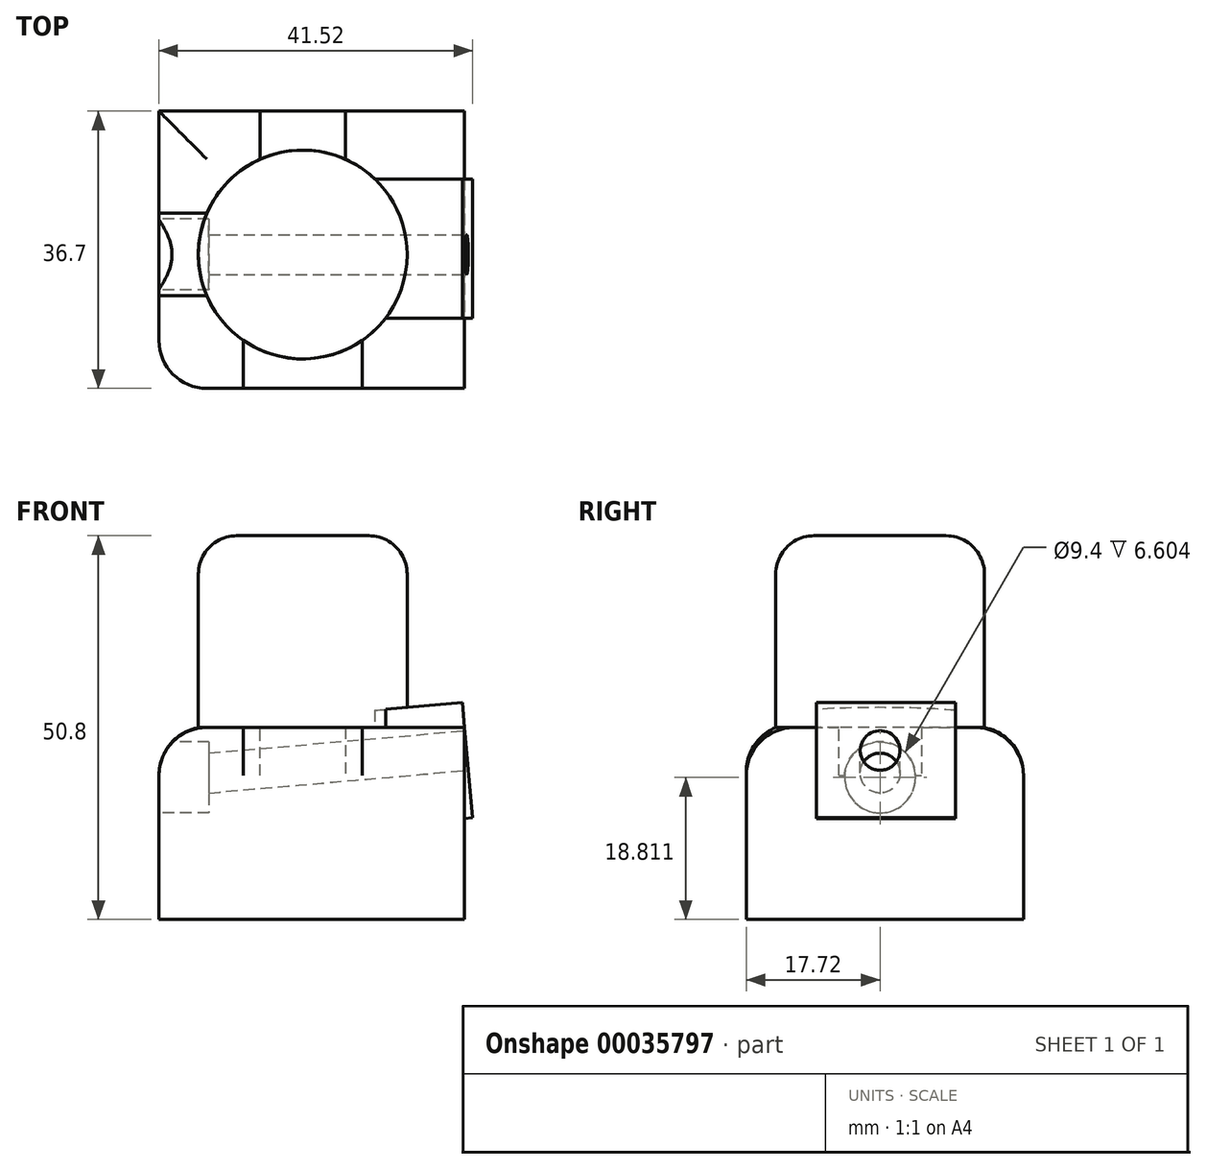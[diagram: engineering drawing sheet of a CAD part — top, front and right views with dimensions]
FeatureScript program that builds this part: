
annotation { "Feature Type Name" : "Feature", "Feature Type Description" : "" }
export const myFeature = defineFeature(function(context is Context, id is Id, definition is map)
    precondition{}
    {
        {
            var Q0;
            Q0=qCreatedBy(makeId("Top.planeOp"),FACE);
            var sketch = newSketch(context, id + "F0", { "sketchPlane" : qUnion([Q0])});
            skLineSegment(sketch, "E0.bottom", {"start": v(-50.18, -17.72) * mm, "end": v(-9.7, -17.72) * mm});
            skLineSegment(sketch, "E0.top", {"start": v(-50.18, 18.98) * mm, "end": v(-9.7, 18.98) * mm});
            skLineSegment(sketch, "E0.left", {"start": v(-50.18, -17.72) * mm, "end": v(-50.18, 18.98) * mm});
            skLineSegment(sketch, "E0.right", {"start": v(-9.7, -17.72) * mm, "end": v(-9.7, 18.98) * mm});
            skSolve(sketch);
        }
        {
            var Q0;
            Q0 = qSketchRegion(id + "F0", true);
            extrude(context, id + "F1", {"entities" : qUnion([Q0]), "depth" : 25.4 * mm});
        }
        {
            var Q0;
            Q0=makeQuery(id+"F1.opExtrude","CAP_FACE",FACE,{"disambiguationData":[OSD([sQuery(id+"F0.wireOp",EDGE,"E0.bottom"),sQuery(id+"F0.wireOp",EDGE,"E0.top"),sQuery(id+"F0.wireOp",EDGE,"E0.left"),sQuery(id+"F0.wireOp",EDGE,"E0.right")])],"isStart":false});
            var sketch = newSketch(context, id + "F2", { "sketchPlane" : qUnion([Q0])});
            skCircle(sketch, "E1", {"center": v(-31.13, 0) * mm, "radius": 13.82 * mm});
            skCircle(sketch, "E2", {"center": v(35.07, -59.3) * mm, "radius": 14.6 * mm});
            skSolve(sketch);
        }
        {
            var Q0;
            Q0=makeQuery(id+"F2.imprint","IMPRINT",FACE,{"disambiguationData":[TD([[makeQuery(id+"F2.imprint","IMPRINT",EDGE,{"derivedFrom":sQuery(id+"F2.wireOp",EDGE,"E1")}),1.0]])]});
            extrude(context, id + "F3", {"entities" : qUnion([Q0]), "operationType" : NewBodyOperationType.ADD, "depth" : 25.4 * mm});
        }
        {
            var Q0;
            Q0=makeQuery(id+"F1.opExtrude","CAP_EDGE",EDGE,{"disambiguationData":[OSD([sQuery(id+"F0.wireOp",EDGE,"E0.right")])],"isStart":false});
            cPlane(context, id + "F4", {"entities" : qUnion([Q0]), "cplaneType" : CPlaneType.LINE_ANGLE, "offset" : 25.4 * mm, "angle" : 265 * degree, "width" : 152.4 * mm, "height" : 152.4 * mm});
        }
        {
            var Q0;
            Q0=qCreatedBy(id+"F4.planeOp",FACE);
            var sketch = newSketch(context, id + "F5", { "sketchPlane" : qUnion([Q0])});
            skLineSegment(sketch, "E3.bottom", {"start": v(8.4, 14.18) * mm, "end": v(-10, 14.18) * mm});
            skLineSegment(sketch, "E3.top", {"start": v(8.4, 29.46) * mm, "end": v(-10, 29.46) * mm});
            skLineSegment(sketch, "E3.left", {"start": v(8.4, 14.18) * mm, "end": v(8.4, 29.46) * mm});
            skLineSegment(sketch, "E3.right", {"start": v(-10, 14.18) * mm, "end": v(-10, 29.46) * mm});
            skSolve(sketch);
        }
        {
            var Q0;
            Q0=makeQuery(id+"F1.opExtrude","CAP_EDGE",EDGE,{"disambiguationData":[OSD([sQuery(id+"F0.wireOp",EDGE,"E0.bottom")])],"isStart":false});
            fillet(context, id + "F6", {"entities" : qUnion([Q0]), "radius" : 6.35 * mm, "tangentPropagation" : true, "allowEdgeOverflow" : false});
        }
        {
            var Q0;
            Q0 = qSketchRegion(id + "F5", true);
            extrude(context, id + "F7", {"entities" : qUnion([Q0]), "operationType" : NewBodyOperationType.ADD, "depth" : 25.4 * mm, "offsetDistance" : 25.4 * mm});
        }
        {
            var Q0;
            Q0=makeQuery(id+"F7.opExtrude","CAP_FACE",FACE,{"disambiguationData":[OSD([sQuery(id+"F5.wireOp",EDGE,"E3.bottom"),sQuery(id+"F5.wireOp",EDGE,"E3.top"),sQuery(id+"F5.wireOp",EDGE,"E3.left"),sQuery(id+"F5.wireOp",EDGE,"E3.right")])],"isStart":true});
            var sketch = newSketch(context, id + "F8", { "sketchPlane" : qUnion([Q0])});
            skCircle(sketch, "E4", {"center": v(0, 23.11) * mm, "radius": 2.63 * mm});
            skSolve(sketch);
        }
        {
            var Q0;
            Q0 = qSketchRegion(id + "F8", true);
            extrude(context, id + "F9", {"entities" : qUnion([Q0]), "operationType" : NewBodyOperationType.REMOVE, "endBound" : BoundingType.THROUGH_ALL, "oppositeDirection" : true, "depth" : 25.4 * mm, "offsetDistance" : 25.4 * mm});
        }
        {
            var Q0;
            Q0=makeQuery(id+"F1.opExtrude","CAP_EDGE",EDGE,{"disambiguationData":[OSD([sQuery(id+"F0.wireOp",EDGE,"E0.top")])],"isStart":false});
            var Q1;
            Q1=makeQuery(id+"F1.opExtrude","CAP_EDGE",EDGE,{"disambiguationData":[OSD([sQuery(id+"F0.wireOp",EDGE,"E0.left")])],"isStart":false});
            fillet(context, id + "F10", {"entities" : qUnion([Q0, Q1]), "radius" : 6.35 * mm, "tangentPropagation" : true, "allowEdgeOverflow" : false});
        }
        {
            var Q0;
            Q0=makeQuery(id+"F1.opExtrude","SWEPT_FACE",FACE,{"disambiguationData":[OSD([sQuery(id+"F0.wireOp",EDGE,"E0.left")])]});
            var sketch = newSketch(context, id + "F11", { "sketchPlane" : qUnion([Q0])});
            skCircle(sketch, "E5", {"center": v(0, 18.81) * mm, "radius": 4.7 * mm});
            skSolve(sketch);
        }
        {
            var Q0;
            {var subQ1=sQuery(id+"F0.wireOp",EDGE,"E0.left");var subQ2=makeQuery(id+"F1.opExtrude","SWEPT_FACE",FACE,{"disambiguationData":[OSD([subQ1])]});var subQ9=makeQuery(id+"F9.boolean.opBoolean","INTERSECT",EDGE,{"derivedFrom":[subQ2,makeQuery(id+"F9.opExtrude","SWEPT_FACE",FACE,{"disambiguationData":[OSD([sQuery(id+"F8.wireOp",EDGE,"E4")])]})]});Q0=makeQuery(id+"F11.imprint","IMPRINT",FACE,{"disambiguationData":[TD([[makeQuery(id+"F11.imprint","IMPRINT",EDGE,{"derivedFrom":subQ9}),1.0]])]});}
            var Q1;
            {var subQ1=sQuery(id+"F0.wireOp",EDGE,"E0.left");var subQ2=makeQuery(id+"F1.opExtrude","SWEPT_FACE",FACE,{"disambiguationData":[OSD([subQ1])]});var subQ9=makeQuery(id+"F9.boolean.opBoolean","INTERSECT",EDGE,{"derivedFrom":[subQ2,makeQuery(id+"F9.opExtrude","SWEPT_FACE",FACE,{"disambiguationData":[OSD([sQuery(id+"F8.wireOp",EDGE,"E4")])]})]});Q1=makeQuery(id+"F11.imprint","IMPRINT",FACE,{"disambiguationData":[TD([[makeQuery(id+"F11.imprint","IMPRINT",EDGE,{"derivedFrom":subQ9}),-1.0]])]});}
            extrude(context, id + "F12", {"entities" : qUnion([Q0, Q1]), "operationType" : NewBodyOperationType.REMOVE, "oppositeDirection" : true, "depth" : 6.6 * mm, "offsetDistance" : 25.4 * mm});
        }
        {
            var Q0;
            Q0=makeQuery(id+"F3.opExtrude","CAP_EDGE",EDGE,{"disambiguationData":[OSD([sQuery(id+"F2.wireOp",EDGE,"E1")])],"isStart":false});
            fillet(context, id + "F13", {"entities" : qUnion([Q0]), "tangentPropagation" : true, "radius" : 5.08 * mm, "defaultsChanged" : false, "vertexSettings" : [], "allowEdgeOverflow" : false});
        }
    });
